# Revit family: 701320001_Push_ Pico Seguridad
name_source: partatom
category: Plumbing Fixtures
units: mm (PartAtom-declared; Revit-internal decimal feet)

## family parameters
Always vertical = Yes
Cut with Voids When Loaded = No
Host = Wall
OmniClass Number = 23.31.11.00
OmniClass Title = Faucets
Part Type = Normal
Room Calculation Point = No
Round Connector Dimension = Use Diameter
Shared = No

## types (1)
- Type 1
    Alto = 74 mm  [stored 0.242782 ft]
    Ancho = 74 mm  [stored 0.242782 ft]
    Ciclo de Vida y Desempeño de la Descarga = 150,000 ciclos.
    Default Elevation = 0 mm  [stored 0 ft]
    Description = Nuestra grifería de lavamanos antivandálica viene con pico de seguridad y accionamiento tipo push. Con cierre automático temporizado
    Flujo Maximo por Norma = 9,68 L/min - 0,49 L/Descarga
    Flujo Real (L/min) = 6,5 - 9,68 L/min - 0,33 - 0,49 L/Descarga
    Garantía = 1 Año
    Manufacturer = Corona
    Material = Corona_Aluminio
    Material 2 = Corona_Cobre
    Model = Push Pico de Seguridad
    Presion Maxima Recomendada = 80 psi
    Presion Minima Recomendada = 20 psi
    Profundidad = 61 mm  [stored 0.200131 ft]
    Referencia = 701320001
    URL = https://corona.co

note: [stored X ft] marks values corroborated as IEEE doubles in the binary element streams (Revit-internal decimal feet)

## geometry (parser evidence)
native form markers: Sweep x7
no freeform markers — native parametric forms only
